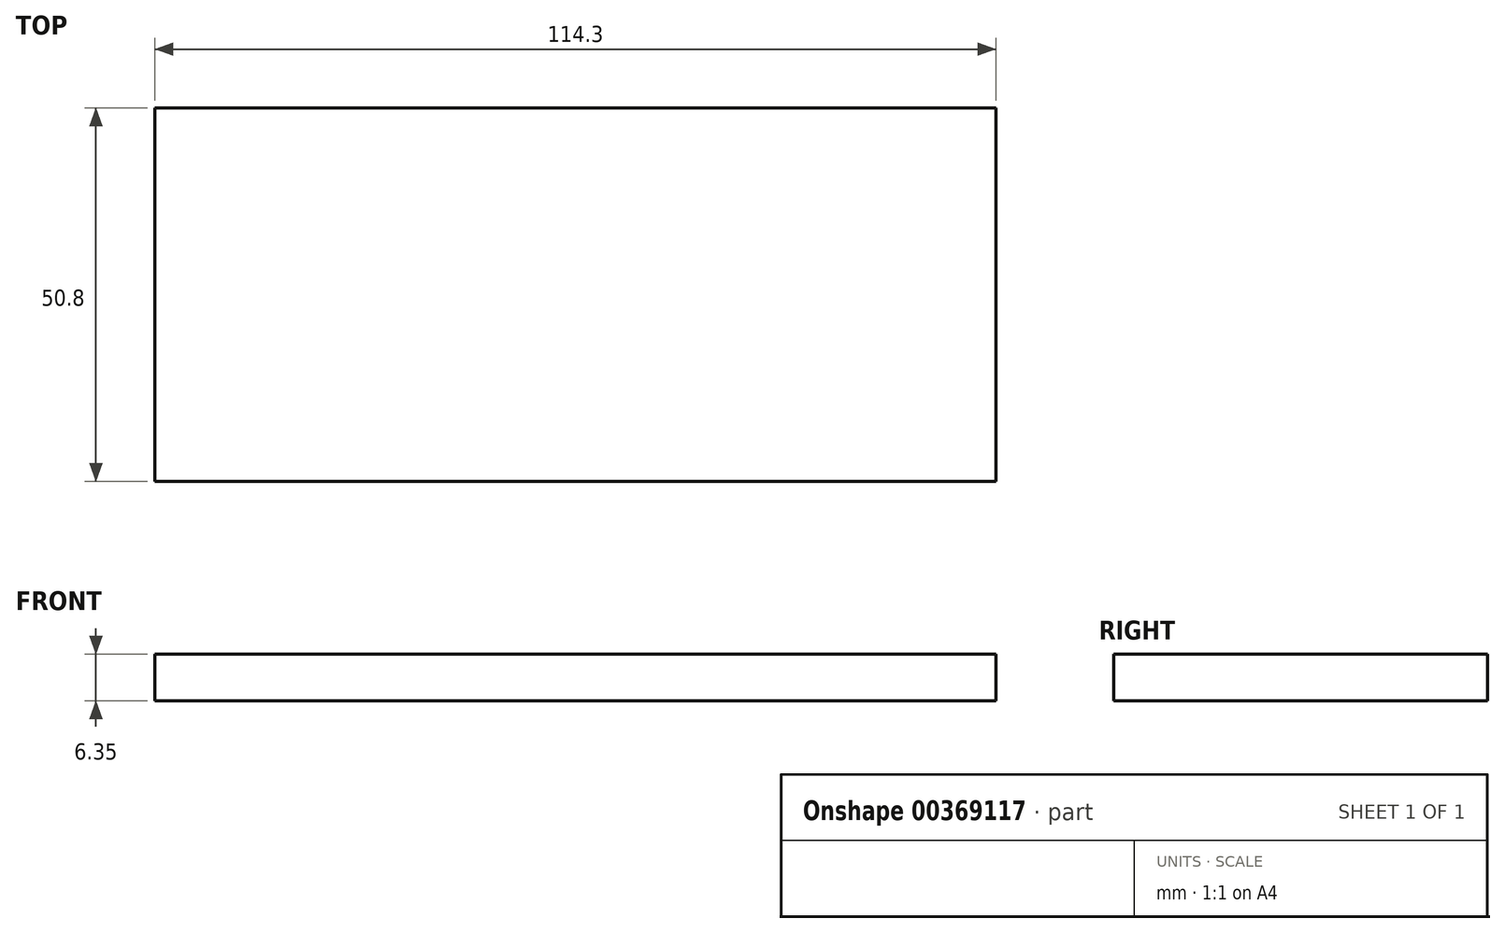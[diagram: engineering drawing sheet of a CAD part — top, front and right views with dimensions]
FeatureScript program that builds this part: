
annotation { "Feature Type Name" : "Feature", "Feature Type Description" : "" }
export const myFeature = defineFeature(function(context is Context, id is Id, definition is map)
    precondition{}
    {
        {
            var Q0;
            Q0=qCreatedBy(makeId("Top.planeOp"),FACE);
            var sketch = newSketch(context, id + "F0", { "sketchPlane" : qUnion([Q0])});
            skLineSegment(sketch, "E0.bottom", {"start": v(0, 0) * mm, "end": v(114.3, 0) * mm});
            skLineSegment(sketch, "E0.top", {"start": v(0, -50.8) * mm, "end": v(114.3, -50.8) * mm});
            skLineSegment(sketch, "E0.left", {"start": v(0, 0) * mm, "end": v(0, -50.8) * mm});
            skLineSegment(sketch, "E0.right", {"start": v(114.3, 0) * mm, "end": v(114.3, -50.8) * mm});
            skSolve(sketch);
        }
        {
            var Q0;
            Q0=makeQuery(id+"F0.imprint","IMPRINT",FACE,{"disambiguationData":[TD([[makeQuery(id+"F0.imprint","IMPRINT",EDGE,{"derivedFrom":sQuery(id+"F0.wireOp",EDGE,"E0.bottom")}),-1.0]])]});
            extrude(context, id + "F1", {"entities" : qUnion([Q0]), "depth" : 6.35 * mm});
        }
    });
